# Revit family: MI-O-BO
name_source: partatom
category: Plumbing Fixtures
revit_build: Autodesk Revit 2018 (Build: 20170223_1515(x64)
units: mm (PartAtom-declared; Revit-internal decimal feet)

## family parameters
Always vertical = Yes
Cut with Voids When Loaded = No
Part Type = Normal
Room Calculation Point = No
Round Connector Dimension = Use Diameter
Shared = No
Work Plane-Based = No

## types (17) — shared parameters
Description = 10 to 500 US G.P.M. OIL INTERCEPTOR
E- Height = 6 "
Manufacturer = MIFAB
URL = WWW.MIFAB.COM

## per-type parameters (varying)
| type | A-Length | B- Width |
| MI-O-1 | 28 " | 22 " |
| MI-O-2 | 34 " | 24 " |
| MI-O-3 | 34 " | 24 " |
| MI-O-4 | 48 " | 34 " |
| MI-O-5 | 51 " | 36 " |
| MI-O-6 | 53 " | 36 " |
| MI-O-7 | 58 " | 36 " |
| MI-O-8 | 68 " | 38 " |
| MI-O-9 | 74 " | 40 " |
| MI-O-10 | 78 " | 44 " |
| MI-O-11 | 80 " | 46 " |
| MI-O-12 | 82 " | 48 " |
| MI-O-13 | 84 " | 50 " |
| MI-O-14 | 86 " | 52 " |
| MI-O-A | 21.25 " | 15.75 " |
| MI-O-B | 23.75 " | 15.75 " |
| MI-O-C | 23.75 " | 15.75 " |

note: column(s) folded — value = type name in every type: Model

## geometry (parser evidence)
native form markers: Sweep x2
no freeform markers — native parametric forms only
